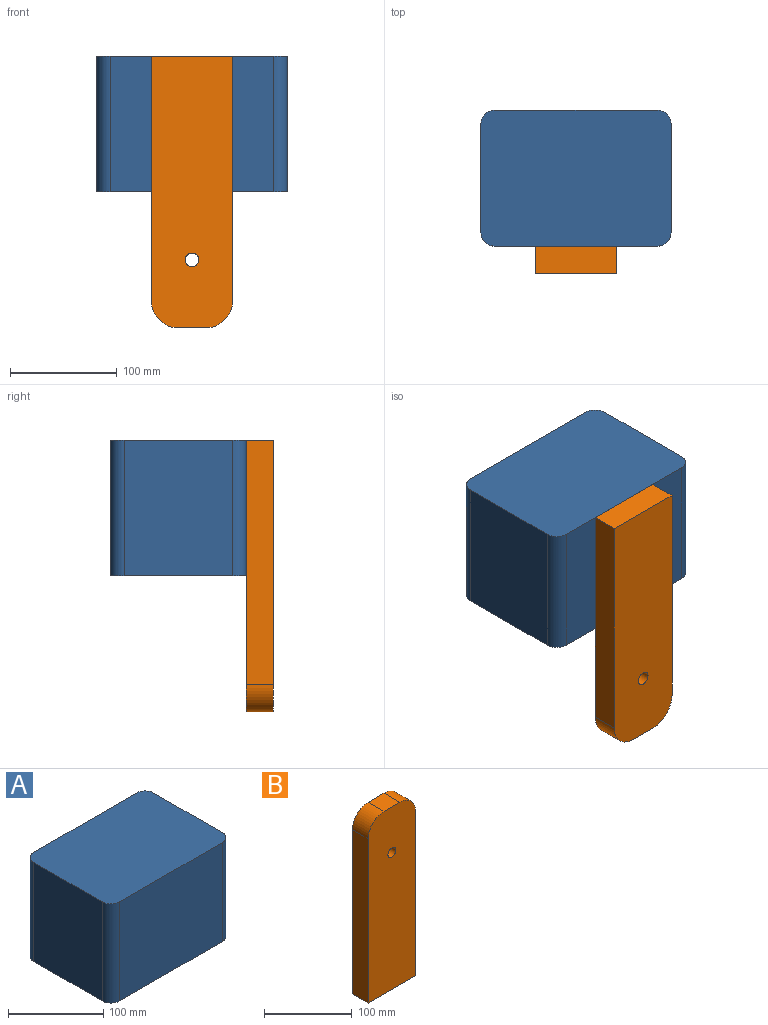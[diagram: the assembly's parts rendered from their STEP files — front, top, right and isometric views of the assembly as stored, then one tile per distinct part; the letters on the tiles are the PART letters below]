
ASSEMBLY  parts=2 mates=3
PART A: 19 faces, bbox 177.8x127x127 mm
  f0: plane 177.8x127mm, normal (0,0,-1), area 12903.2mm2, adj f1,f2,f3,f4,f6,f7,f8,f9
  f1: plane 152.4x127mm, normal (0,-1,0), area 19354.8mm2, adj f0,f5,f15,f18
  f2: plane 127x101.6mm, normal (1,0,0), area 12903.2mm2, adj f0,f5,f15,f16
  f3: plane 152.4x127mm, normal (0,1,0), area 19354.8mm2, adj f0,f5,f16,f17
  f4: plane 127x101.6mm, normal (-1,0,0), area 12903.2mm2, adj f0,f5,f17,f18
  f5: plane 177.8x127mm, normal (0,0,1), area 22442.1mm2, adj f1,f2,f3,f4,f15,f16,f17,f18
  f6: plane 101.6x50.8mm, normal (-1,0,0), area 5161.3mm2, adj f0,f10,f11,f14
  f7: plane 101.6x101.6mm, normal (0,-1,0), area 10322.6mm2, adj f0,f10,f11,f12
  f8: plane 101.6x50.8mm, normal (1,0,0), area 5161.3mm2, adj f0,f10,f12,f13
  f9: plane 101.6x101.6mm, normal (0,1,0), area 10322.6mm2, adj f0,f10,f13,f14
  f10: plane 127x76.2mm, normal (0,0,-1), area 9538.9mm2, adj f6,f7,f8,f9,f11,f12,f13,f14
  f11: cylinder r=12.7mm len=101.6mm, axis (0,0,1), area 2026.8mm2, adj f0,f6,f7,f10
  f12: cylinder r=12.7mm len=101.6mm, axis (0,0,-1), area 2026.8mm2, adj f0,f7,f8,f10
  f13: cylinder r=12.7mm len=101.6mm, axis (0,0,1), area 2026.8mm2, adj f0,f8,f9,f10
  f14: cylinder r=12.7mm len=101.6mm, axis (0,0,-1), area 2026.8mm2, adj f0,f6,f9,f10
  f15: cylinder r=12.7mm len=127mm, axis (0,0,-1), area 2533.5mm2, adj f0,f1,f2,f5
  f16: cylinder r=12.7mm len=127mm, axis (0,0,1), area 2533.5mm2, adj f0,f2,f3,f5
  f17: cylinder r=12.7mm len=127mm, axis (0,0,-1), area 2533.5mm2, adj f0,f3,f4,f5
  f18: cylinder r=12.7mm len=127mm, axis (0,0,1), area 2533.5mm2, adj f0,f1,f4,f5
PART B: 9 faces, bbox 76.2x25.4x254 mm
  f0: plane 228.6x25.4mm, normal (1,0,0), area 5806.4mm2, adj f1,f3,f5,f7
  f1: plane 254x76.2mm, normal (0,1,0), area 18951.2mm2, adj f0,f2,f4,f5,f6,f7,f8
  f2: plane 228.6x25.4mm, normal (-1,0,0), area 5806.4mm2, adj f1,f3,f5,f6
  f3: plane 254x76.2mm, normal (0,-1,0), area 18951.2mm2, adj f0,f2,f4,f5,f6,f7,f8
  f4: plane 25.4x25.4mm, normal (0,0,1), area 645.2mm2, adj f1,f3,f6,f7
  f5: plane 76.2x25.4mm, normal (0,0,-1), area 1935.5mm2, adj f0,f1,f2,f3
  f6: cylinder r=25.4mm len=25.4mm, axis (0,1,0), area 1013.4mm2, adj f1,f2,f3,f4
  f7: cylinder r=25.4mm len=25.4mm, axis (0,-1,0), area 1013.4mm2, adj f0,f1,f3,f4
  f8: cylinder r=6.35mm len=25.4mm, axis (0,1,0), area 1013.4mm2, adj f1,f3
PLACE A t=(-86.6,-187.79,243.4)mm fixed
PLACE B rot(axis=(0,1,0),180deg) t=(-40.94,-325.15,370.4)mm
MATE planar B.f5 <-> A.f5  axis (0,0,1) through (-79.04,-284.09,370.4)mm
MATE planar B.f1 <-> A.f1  axis (0,1,0) through (-79.04,-271.39,370.4)mm
MATE cylindrical A.f3 <-> B.f3  axis (0,1,0) through (-79.04,-144.39,370.4)mm
